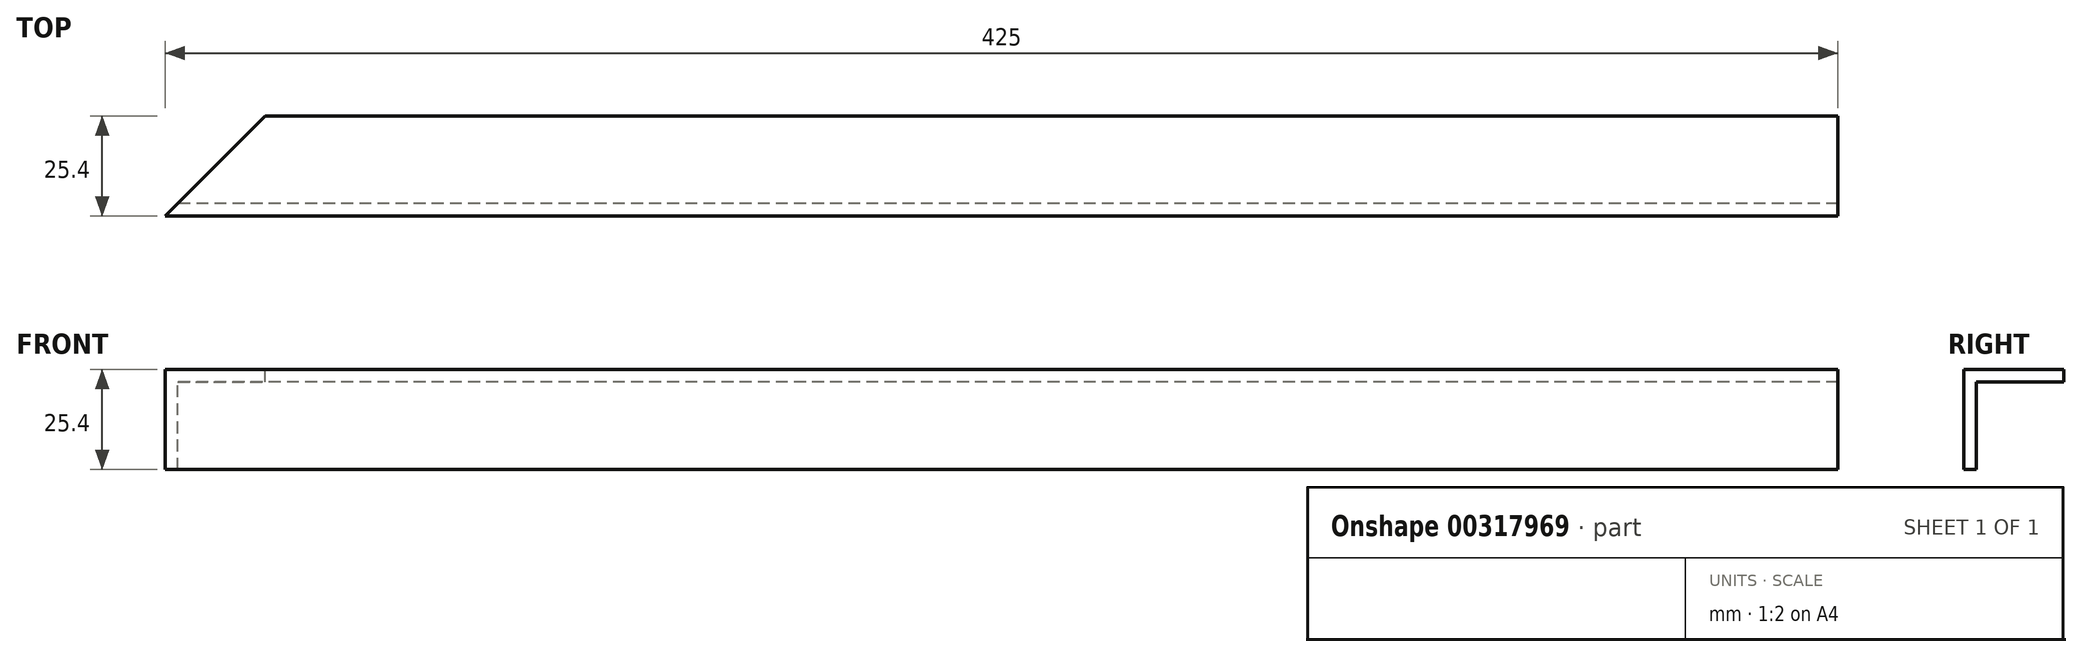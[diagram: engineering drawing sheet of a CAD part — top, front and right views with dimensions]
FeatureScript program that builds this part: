
annotation { "Feature Type Name" : "Feature", "Feature Type Description" : "" }
export const myFeature = defineFeature(function(context is Context, id is Id, definition is map)
    precondition{}
    {
        {
            var Q0;
            Q0=qCreatedBy(makeId("Right.planeOp"),FACE);
            var sketch = newSketch(context, id + "F0", { "sketchPlane" : qUnion([Q0])});
            skLineSegment(sketch, "E0", {"start": v(0, -10.12) * mm, "end": v(0, 15.28) * mm});
            skLineSegment(sketch, "E1", {"start": v(0, 15.28) * mm, "end": v(25.4, 15.28) * mm});
            skLineSegment(sketch, "E2.0", {"start": v(3.2, 12.08) * mm, "end": v(25.4, 12.08) * mm});
            skLineSegment(sketch, "E2.1", {"start": v(3.2, -10.12) * mm, "end": v(3.2, 12.08) * mm});
            skLineSegment(sketch, "E3", {"start": v(0, -10.12) * mm, "end": v(3.2, -10.12) * mm});
            skLineSegment(sketch, "E4", {"start": v(25.4, 12.08) * mm, "end": v(25.4, 15.28) * mm});
            skSolve(sketch);
        }
        {
            var Q0;
            Q0=makeQuery(id+"F0.imprint","IMPRINT",FACE,{"disambiguationData":[TD([[makeQuery(id+"F0.imprint","IMPRINT",EDGE,{"derivedFrom":sQuery(id+"F0.wireOp",EDGE,"E0")}),-1.0]])]});
            var Q1;
            Q1=sQuery(id+"F0.wireOp",EDGE,"E2.0");
            var Q2;
            Q2=sQuery(id+"F0.wireOp",EDGE,"E2.1");
            var Q3;
            Q3=sQuery(id+"F0.wireOp",EDGE,"E3");
            var Q4;
            Q4=sQuery(id+"F0.wireOp",EDGE,"E0");
            var Q5;
            Q5=sQuery(id+"F0.wireOp",EDGE,"E1");
            var Q6;
            Q6=sQuery(id+"F0.wireOp",EDGE,"E4");
            extrude(context, id + "F1", {"entities" : qUnion([Q0]), "surfaceEntities" : qUnion([Q1, Q2, Q3, Q4, Q5, Q6]), "endBound" : BoundingType.SYMMETRIC, "depth" : 425 * mm});
        }
        {
            var Q0;
            Q0=makeQuery(id+"F1.opExtrude","SWEPT_FACE",FACE,{"disambiguationData":[OSD([sQuery(id+"F0.wireOp",EDGE,"E1")])]});
            var sketch = newSketch(context, id + "F2", { "sketchPlane" : qUnion([Q0])});
            skLineSegment(sketch, "E5", {"start": v(-212.5, 0) * mm, "end": v(-187.1, 25.4) * mm});
            skLineSegment(sketch, "E6", {"start": v(-187.1, 25.4) * mm, "end": v(-212.5, 25.4) * mm});
            skLineSegment(sketch, "E7", {"start": v(-212.5, 0) * mm, "end": v(-173.11, 0) * mm, "construction": true});
            skLineSegment(sketch, "E8", {"start": v(-212.5, 25.4) * mm, "end": v(-212.5, 0) * mm});
            skSolve(sketch);
        }
        {
            var Q0;
            Q0 = qSketchRegion(id + "F2", true);
            extrude(context, id + "F3", {"entities" : qUnion([Q0]), "operationType" : NewBodyOperationType.REMOVE, "oppositeDirection" : true, "depth" : 25.4 * mm});
        }
    });
